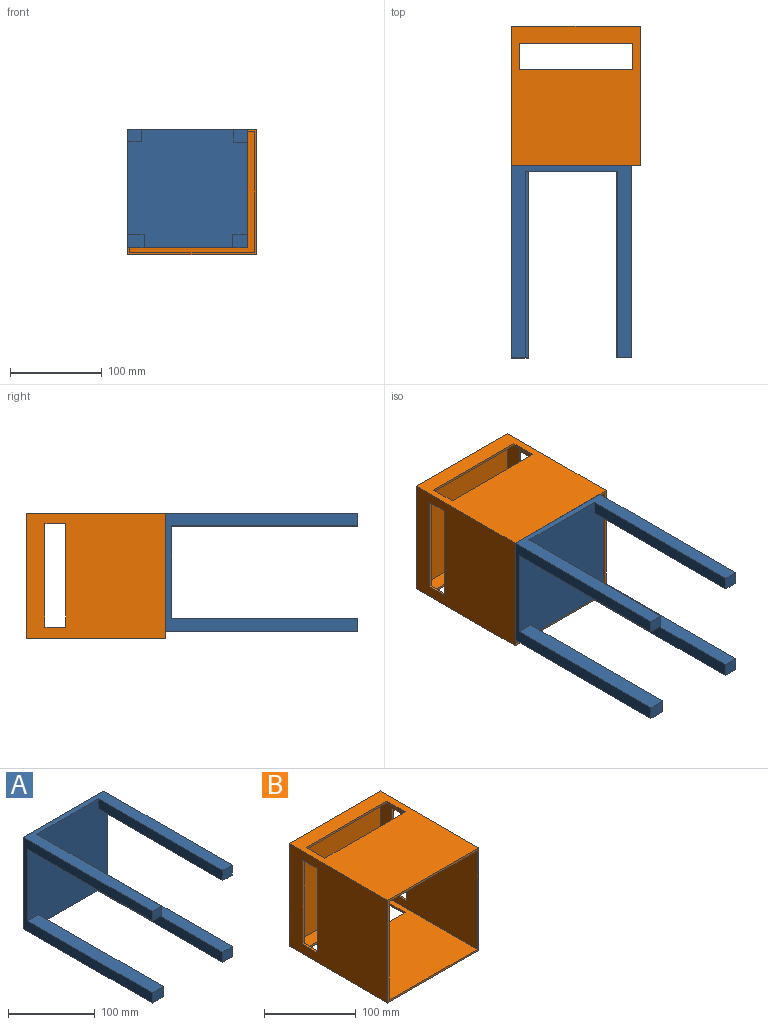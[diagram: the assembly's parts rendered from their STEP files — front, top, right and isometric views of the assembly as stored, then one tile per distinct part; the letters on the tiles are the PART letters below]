
ASSEMBLY  parts=2 mates=1
PART A: 19 faces, bbox 130.8x209.6x129.4 mm
  f0: plane 130.77x129.4mm, normal (0,-1,0), area 16009mm2, adj f1,f2,f3,f4,f6,f7,f9,f10
  f1: plane 209.55x130.77mm, normal (0,0,-1), area 4495.4mm2, adj f0,f2,f4,f5,f17,f18
  f2: plane 209.55x129.4mm, normal (1,0,0), area 6620.6mm2, adj f0,f1,f3,f5,f9,f11,f12,f13
  f3: plane 209.55x130.77mm, normal (0,0,1), area 7005.1mm2, adj f0,f2,f4,f5,f7,f8,f10,f11
  f4: plane 209.55x129.4mm, normal (-1,0,0), area 6505.5mm2, adj f0,f1,f3,f5,f6,f8,f16,f18
  f5: plane 130.77x129.4mm, normal (0,1,0), area 16921.5mm2, adj f1,f2,f3,f4
  f6: plane 203.2x15.09mm, normal (0,0,-1), area 3065.5mm2, adj f0,f4,f7,f8
  f7: plane 203.2x13.61mm, normal (1,0,0), area 2764.8mm2, adj f0,f3,f6,f8
  f8: plane 15.09x13.61mm, normal (0,-1,0), area 205.3mm2, adj f3,f4,f6,f7
  f9: plane 203.2x15.3mm, normal (0,0,-1), area 3109.2mm2, adj f0,f2,f10,f11
  f10: plane 203.2x14.12mm, normal (-1,0,0), area 2869.6mm2, adj f0,f3,f9,f11
  f11: plane 15.3x14.12mm, normal (0,-1,0), area 216.1mm2, adj f2,f3,f9,f10
  f12: plane 203.2x16.1mm, normal (0,0,-1), area 3271.1mm2, adj f0,f2,f14,f15
  f13: plane 203.2x16.1mm, normal (0,0,1), area 3271.1mm2, adj f0,f2,f14,f15
  f14: plane 203.2x14.42mm, normal (-1,0,0), area 2929.4mm2, adj f0,f12,f13,f15
  f15: plane 16.1x14.42mm, normal (0,-1,0), area 232.1mm2, adj f2,f12,f13,f14
  f16: plane 203.2x18.04mm, normal (0,0,1), area 3665mm2, adj f0,f4,f17,f18
  f17: plane 203.2x14.37mm, normal (1,0,0), area 2919mm2, adj f0,f1,f16,f18
  f18: plane 18.04x14.37mm, normal (0,-1,0), area 259.1mm2, adj f1,f4,f16,f17
PART B: 27 faces, bbox 140.6x152.4x137 mm
  f0: plane 152.4x140.59mm, normal (0,0,-1), area 17873mm2, adj f4,f5,f8,f9,f23,f24,f25,f26
  f1: plane 152.4x140.59mm, normal (0,0,1), area 17873mm2, adj f4,f5,f8,f9,f19,f20,f21,f22
  f2: plane 149.86x135.51mm, normal (0,0,1), area 16754.7mm2, adj f6,f7,f8,f10,f23,f24,f25,f26
  f3: plane 149.86x135.51mm, normal (0,0,-1), area 16754.7mm2, adj f6,f7,f8,f10,f19,f20,f21,f22
  f4: plane 152.4x136.99mm, normal (1,0,0), area 18327.1mm2, adj f0,f1,f8,f9,f15,f16,f17,f18
  f5: plane 152.4x136.99mm, normal (-1,0,0), area 18327.1mm2, adj f0,f1,f8,f9,f11,f12,f13,f14
  f6: plane 149.86x131.91mm, normal (-1,0,0), area 17217.9mm2, adj f2,f3,f8,f10,f15,f16,f17,f18
  f7: plane 149.86x131.91mm, normal (1,0,0), area 17217.9mm2, adj f2,f3,f8,f10,f11,f12,f13,f14
  f8: plane 140.59x136.99mm, normal (0,-1,0), area 1384.3mm2, adj f0,f1,f2,f3,f4,f5,f6,f7
  f9: plane 140.59x136.99mm, normal (0,1,0), area 19258.8mm2, adj f0,f1,f4,f5
  f10: plane 135.51x131.91mm, normal (0,-1,0), area 17874.5mm2, adj f2,f3,f6,f7
  f11: plane 112.6x2.54mm, normal (0,-1,0), area 286mm2, adj f5,f7,f12,f14
  f12: plane 22.64x2.54mm, normal (0,0,1), area 57.5mm2, adj f5,f7,f11,f13
  f13: plane 112.6x2.54mm, normal (0,1,0), area 286mm2, adj f5,f7,f12,f14
  f14: plane 22.64x2.54mm, normal (0,0,-1), area 57.5mm2, adj f5,f7,f11,f13
  f15: plane 22.64x2.54mm, normal (0,0,-1), area 57.5mm2, adj f4,f6,f16,f18
  f16: plane 112.6x2.54mm, normal (0,1,0), area 286mm2, adj f4,f6,f15,f17
  f17: plane 22.64x2.54mm, normal (0,0,1), area 57.5mm2, adj f4,f6,f16,f18
  f18: plane 112.6x2.54mm, normal (0,-1,0), area 286mm2, adj f4,f6,f15,f17
  f19: plane 28.67x2.54mm, normal (-1,0,0), area 72.8mm2, adj f1,f3,f20,f22
  f20: plane 123.94x2.54mm, normal (0,1,0), area 314.8mm2, adj f1,f3,f19,f21
  f21: plane 28.67x2.54mm, normal (1,0,0), area 72.8mm2, adj f1,f3,f20,f22
  f22: plane 123.94x2.54mm, normal (0,-1,0), area 314.8mm2, adj f1,f3,f19,f21
  f23: plane 123.94x2.54mm, normal (0,-1,0), area 314.8mm2, adj f0,f2,f24,f26
  f24: plane 28.67x2.54mm, normal (1,0,0), area 72.8mm2, adj f0,f2,f23,f25
  f25: plane 123.94x2.54mm, normal (0,1,0), area 314.8mm2, adj f0,f2,f24,f26
  f26: plane 28.67x2.54mm, normal (-1,0,0), area 72.8mm2, adj f0,f2,f23,f25
PLACE A t=(-4.91,-152.4,3.79)mm
PLACE B at identity
MATE fastened A.f5 <-> B.f8  axis (0,1,0) through (-70.29,-152.4,68.49)mm
